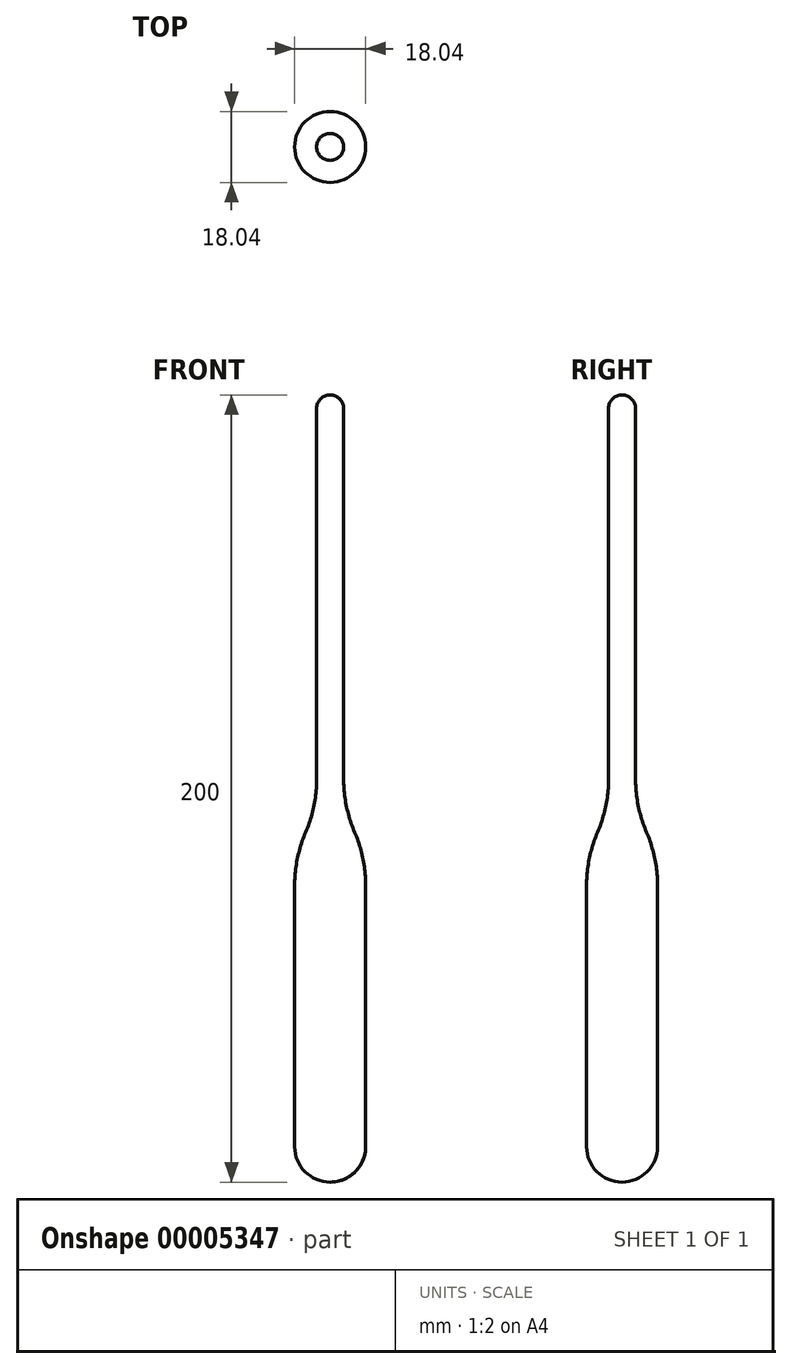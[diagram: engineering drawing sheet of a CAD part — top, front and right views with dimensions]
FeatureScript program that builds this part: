
annotation { "Feature Type Name" : "Feature", "Feature Type Description" : "" }
export const myFeature = defineFeature(function(context is Context, id is Id, definition is map)
    precondition{}
    {
        {
            var Q0;
            Q0=qCreatedBy(makeId("Front.planeOp"),FACE);
            var sketch = newSketch(context, id + "F0", { "sketchPlane" : qUnion([Q0])});
            skLineSegment(sketch, "E0", {"start": v(0, 0) * mm, "end": v(0, 200) * mm});
            skLineSegment(sketch, "E1", {"start": v(3.43, 196.57) * mm, "end": v(3.43, 102.5) * mm});
            skLineSegment(sketch, "E2", {"start": v(9.02, 75.3) * mm, "end": v(9.02, 9.02) * mm});
            skArc(sketch, "E3", {"start": v(3.43, 196.57) * mm, "mid": v(2.42, 199) * mm, "end": v(0, 200) * mm});
            skArc(sketch, "E4", {"start": v(0, 0) * mm, "mid": v(6.38, 2.64) * mm, "end": v(9.02, 9.02) * mm});
            skArc(sketch, "E5", {"start": v(3.43, 102.5) * mm, "mid": v(4.13, 95.56) * mm, "end": v(6.22, 88.9) * mm});
            skArc(sketch, "E6", {"start": v(9.02, 75.3) * mm, "mid": v(8.31, 82.24) * mm, "end": v(6.22, 88.9) * mm});
            skSolve(sketch);
        }
        {
            var Q0;
            Q0=makeQuery(id+"F0.imprint","IMPRINT",FACE,{"disambiguationData":[TD([[makeQuery(id+"F0.imprint","IMPRINT",EDGE,{"derivedFrom":sQuery(id+"F0.wireOp",EDGE,"E0")}),-1.0]])]});
            var Q1;
            Q1=sQuery(id+"F0.wireOp",EDGE,"E0");
            revolve(context, id + "F1", {"entities" : qUnion([Q0]), "axis" : qUnion([Q1]), "revolveType" : RevolveType.FULL});
        }
    });
